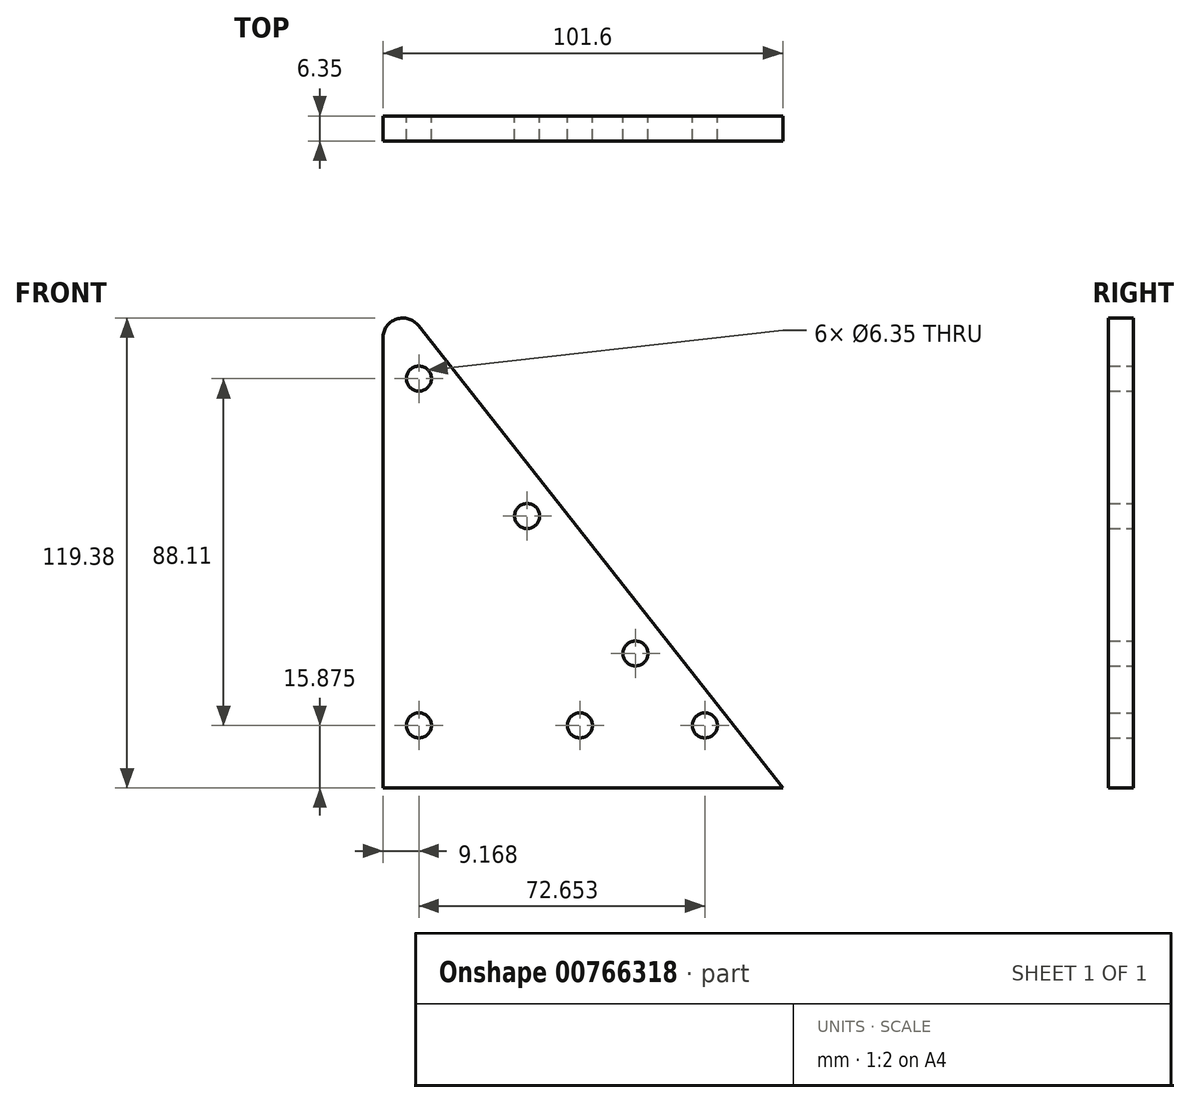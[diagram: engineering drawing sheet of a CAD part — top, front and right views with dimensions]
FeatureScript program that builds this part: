
annotation { "Feature Type Name" : "Feature", "Feature Type Description" : "" }
export const myFeature = defineFeature(function(context is Context, id is Id, definition is map)
    precondition{}
    {
        {
            var Q0;
            Q0=qCreatedBy(makeId("Front.planeOp"),FACE);
            var sketch = newSketch(context, id + "F0", { "sketchPlane" : qUnion([Q0])});
            skLineSegment(sketch, "E0", {"start": v(-52.49, 27.6) * mm, "end": v(-52.49, -86.7) * mm});
            skLineSegment(sketch, "E1", {"start": v(-52.49, -86.7) * mm, "end": v(49.11, -86.7) * mm});
            skLineSegment(sketch, "E2", {"start": v(49.11, -86.7) * mm, "end": v(-43.42, 30.74) * mm});
            skPoint(sketch, "E3.visualSharp", {"position": v(-52.49, 42.26) * mm});
            skArc(sketch, "E3.filletArc", {"start": v(-43.42, 30.74) * mm, "mid": v(-49.07, 32.4) * mm, "end": v(-52.49, 27.6) * mm});
            skSolve(sketch);
        }
        {
            var Q0;
            Q0=makeQuery(id+"F0.imprint","IMPRINT",FACE,{"disambiguationData":[TD([[makeQuery(id+"F0.imprint","IMPRINT",EDGE,{"derivedFrom":sQuery(id+"F0.wireOp",EDGE,"E0")}),1.0]])]});
            var sketch = newSketch(context, id + "F1", { "sketchPlane" : qUnion([Q0])});
            skCircle(sketch, "E4", {"center": v(-43.32, 17.29) * mm, "radius": 3.18 * mm});
            skCircle(sketch, "E5", {"center": v(-15.81, -17.63) * mm, "radius": 3.18 * mm});
            skCircle(sketch, "E6", {"center": v(-43.32, -70.83) * mm, "radius": 3.18 * mm});
            skCircle(sketch, "E7", {"center": v(-2.42, -70.83) * mm, "radius": 3.18 * mm});
            skCircle(sketch, "E8", {"center": v(29.33, -70.83) * mm, "radius": 3.18 * mm});
            skCircle(sketch, "E9", {"center": v(11.7, -52.55) * mm, "radius": 3.18 * mm});
            skSolve(sketch);
        }
        {
            var Q0;
            Q0=makeQuery(id+"F0.imprint","IMPRINT",FACE,{"disambiguationData":[TD([[makeQuery(id+"F0.imprint","IMPRINT",EDGE,{"derivedFrom":sQuery(id+"F0.wireOp",EDGE,"E0")}),1.0]])]});
            extrude(context, id + "F2", {"entities" : qUnion([Q0]), "depth" : 6.35 * mm, "offsetDistance" : 25.4 * mm});
        }
        {
            var Q0;
            Q0=makeQuery(id+"F1.imprint","IMPRINT",FACE,{"disambiguationData":[TD([[makeQuery(id+"F1.imprint","IMPRINT",EDGE,{"derivedFrom":sQuery(id+"F1.wireOp",EDGE,"E8")}),1.0]])]});
            var Q1;
            Q1=makeQuery(id+"F1.imprint","IMPRINT",FACE,{"disambiguationData":[TD([[makeQuery(id+"F1.imprint","IMPRINT",EDGE,{"derivedFrom":sQuery(id+"F1.wireOp",EDGE,"E7")}),1.0]])]});
            var Q2;
            Q2=makeQuery(id+"F1.imprint","IMPRINT",FACE,{"disambiguationData":[TD([[makeQuery(id+"F1.imprint","IMPRINT",EDGE,{"derivedFrom":sQuery(id+"F1.wireOp",EDGE,"E9")}),1.0]])]});
            var Q3;
            Q3=makeQuery(id+"F1.imprint","IMPRINT",FACE,{"disambiguationData":[TD([[makeQuery(id+"F1.imprint","IMPRINT",EDGE,{"derivedFrom":sQuery(id+"F1.wireOp",EDGE,"E5")}),1.0]])]});
            var Q4;
            Q4=makeQuery(id+"F1.imprint","IMPRINT",FACE,{"disambiguationData":[TD([[makeQuery(id+"F1.imprint","IMPRINT",EDGE,{"derivedFrom":sQuery(id+"F1.wireOp",EDGE,"E4")}),1.0]])]});
            var Q5;
            Q5=makeQuery(id+"F1.imprint","IMPRINT",FACE,{"disambiguationData":[TD([[makeQuery(id+"F1.imprint","IMPRINT",EDGE,{"derivedFrom":sQuery(id+"F1.wireOp",EDGE,"E6")}),1.0]])]});
            extrude(context, id + "F3", {"entities" : qUnion([Q0, Q1, Q2, Q3, Q4, Q5]), "operationType" : NewBodyOperationType.REMOVE, "depth" : 43.31 * mm, "offsetDistance" : 25.4 * mm});
        }
    });
